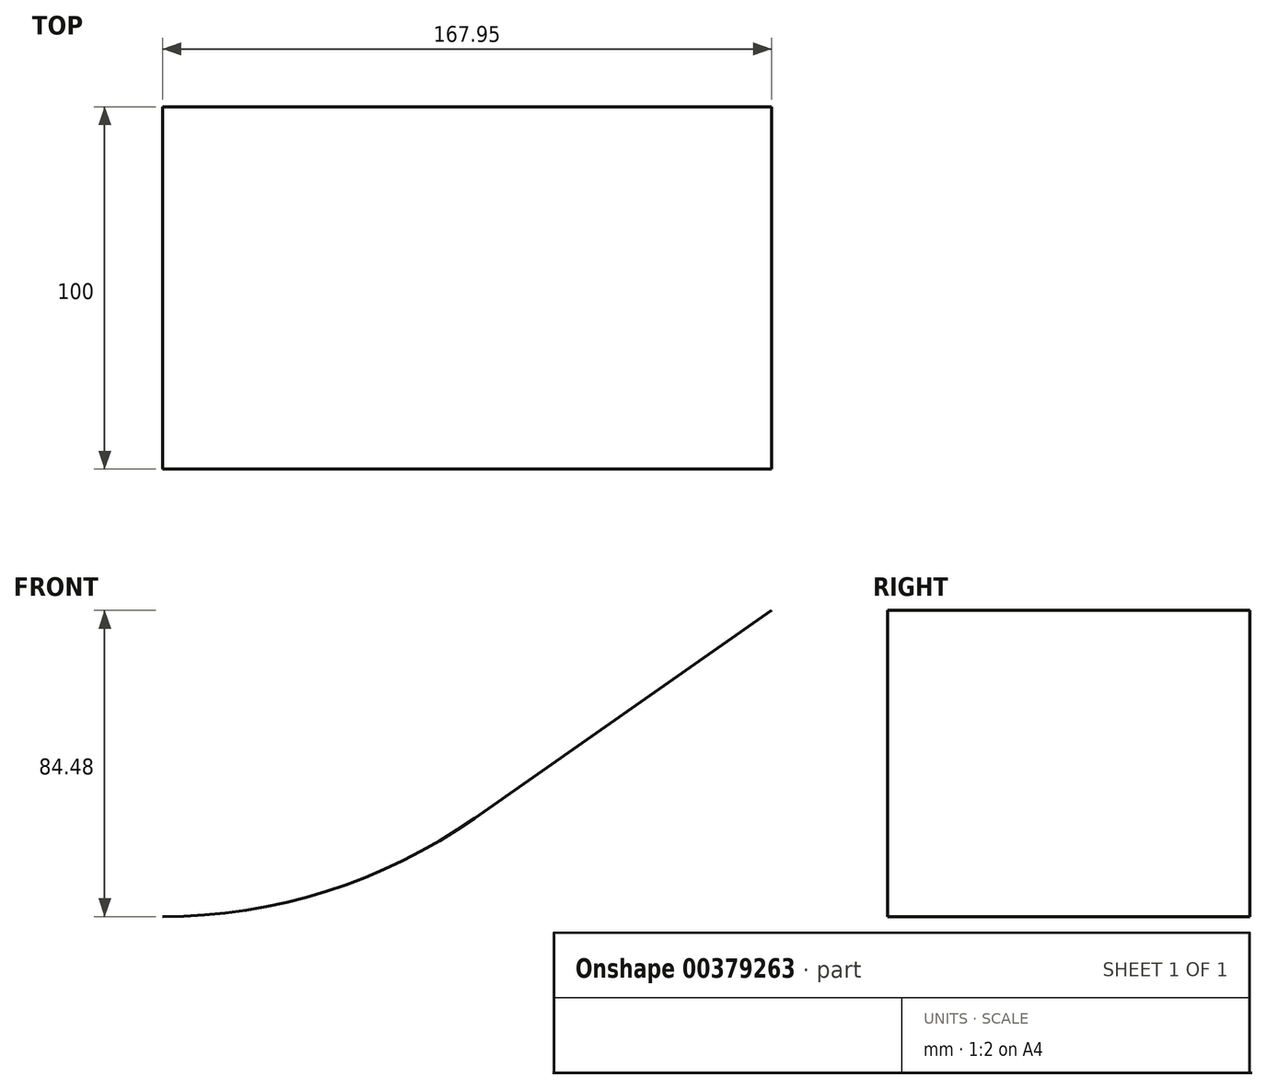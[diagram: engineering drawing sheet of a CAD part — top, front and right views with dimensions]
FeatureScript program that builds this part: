
annotation { "Feature Type Name" : "Feature", "Feature Type Description" : "" }
export const myFeature = defineFeature(function(context is Context, id is Id, definition is map)
    precondition{}
    {
        {
            var Q0;
            Q0=qCreatedBy(makeId("Front.planeOp"),FACE);
            var sketch = newSketch(context, id + "F0", { "sketchPlane" : qUnion([Q0])});
            skArc(sketch, "E0", {"start": v(0, -150) * mm, "mid": v(45.1, -143.06) * mm, "end": v(86.04, -122.87) * mm});
            skLineSegment(sketch, "E1", {"start": v(86.04, -122.87) * mm, "end": v(167.95, -65.52) * mm});
            skLineSegment(sketch, "E2", {"start": v(0, 0) * mm, "end": v(107.12, -153) * mm, "construction": true});
            skSolve(sketch);
        }
        {
            var Q0;
            Q0 = qSketchRegion(id + "F0", true);
            var Q1;
            Q1 = qConstructionFilter(qBodyType(qCreatedBy(id + "F0" ,EDGE), BodyType.WIRE), ConstructionObject.NO);
            extrude(context, id + "F1", {"entities" : qUnion([Q0]), "bodyType" : ToolBodyType.SURFACE, "surfaceEntities" : qUnion([Q1]), "depth" : 100 * mm});
        }
    });
